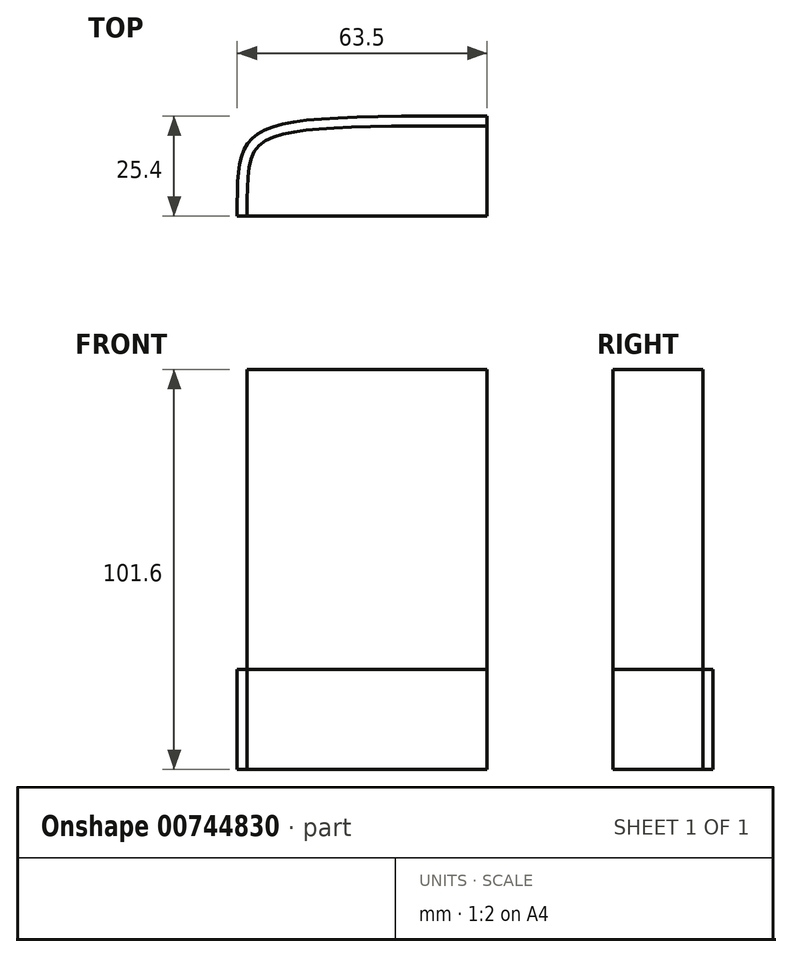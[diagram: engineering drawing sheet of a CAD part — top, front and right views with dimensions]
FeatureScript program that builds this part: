
annotation { "Feature Type Name" : "Feature", "Feature Type Description" : "" }
export const myFeature = defineFeature(function(context is Context, id is Id, definition is map)
    precondition{}
    {
        {
            var Q0;
            Q0=qCreatedBy(makeId("Top.planeOp"),FACE);
            var sketch = newSketch(context, id + "F0", { "sketchPlane" : qUnion([Q0])});
            skLineSegment(sketch, "E0.bottom", {"start": v(0, 0) * mm, "end": v(-63.5, 0) * mm});
            skLineSegment(sketch, "E0.left", {"start": v(0, 0) * mm, "end": v(0, 25.4) * mm});
            skFitSpline(sketch, "E1", {"points": [v(-63.5, 0) * mm, v(0, 25.4) * mm], "startDerivative": vector(0, 76.2) * mm, "endDerivative": vector(190.5, 0) * mm});
            skFitSpline(sketch, "E2.0", {"points": [v(-60.96, 0) * mm, v(-60.96, 1.59) * mm, v(-60.96, 4.55) * mm, v(-60.87, 8.36) * mm, v(-60.6, 11.55) * mm, v(-60.1, 14.1) * mm, v(-59.35, 16.06) * mm, v(-58.33, 17.54) * mm, v(-56.9, 18.78) * mm, v(-54.76, 19.9) * mm, v(-51.76, 20.84) * mm, v(-47.8, 21.58) * mm, v(-42.84, 22.12) * mm, v(-34.77, 22.61) * mm, v(-21.82, 22.86) * mm, v(-7.94, 22.86) * mm, v(0, 22.86) * mm]});
            skSolve(sketch);
        }
        {
            var Q0;
            {var subQ3=sQuery(id+"F0.wireOp",EDGE,"E2.0");Q0=makeQuery(id+"F0.imprint","IMPRINT",FACE,{"disambiguationData":[TD([[makeQuery(id+"F0.imprint","IMPRINT",EDGE,{"derivedFrom":subQ3}),-1.0]])]});}
            extrude(context, id + "F1", {"entities" : qUnion([Q0]), "depth" : 76.2 * mm, "offsetDistance" : 25.4 * mm});
        }
        {
            var Q0;
            {var subQ0=sQuery(id+"F0.wireOp",EDGE,"E1");Q0=makeQuery(id+"F0.imprint","IMPRINT",FACE,{"disambiguationData":[TD([[makeQuery(id+"F0.imprint","IMPRINT",EDGE,{"derivedFrom":subQ0}),-1.0]])]});}
            extrude(context, id + "F2", {"entities" : qUnion([Q0]), "oppositeDirection" : true, "depth" : 25.4 * mm, "offsetDistance" : 25.4 * mm});
        }
    });
